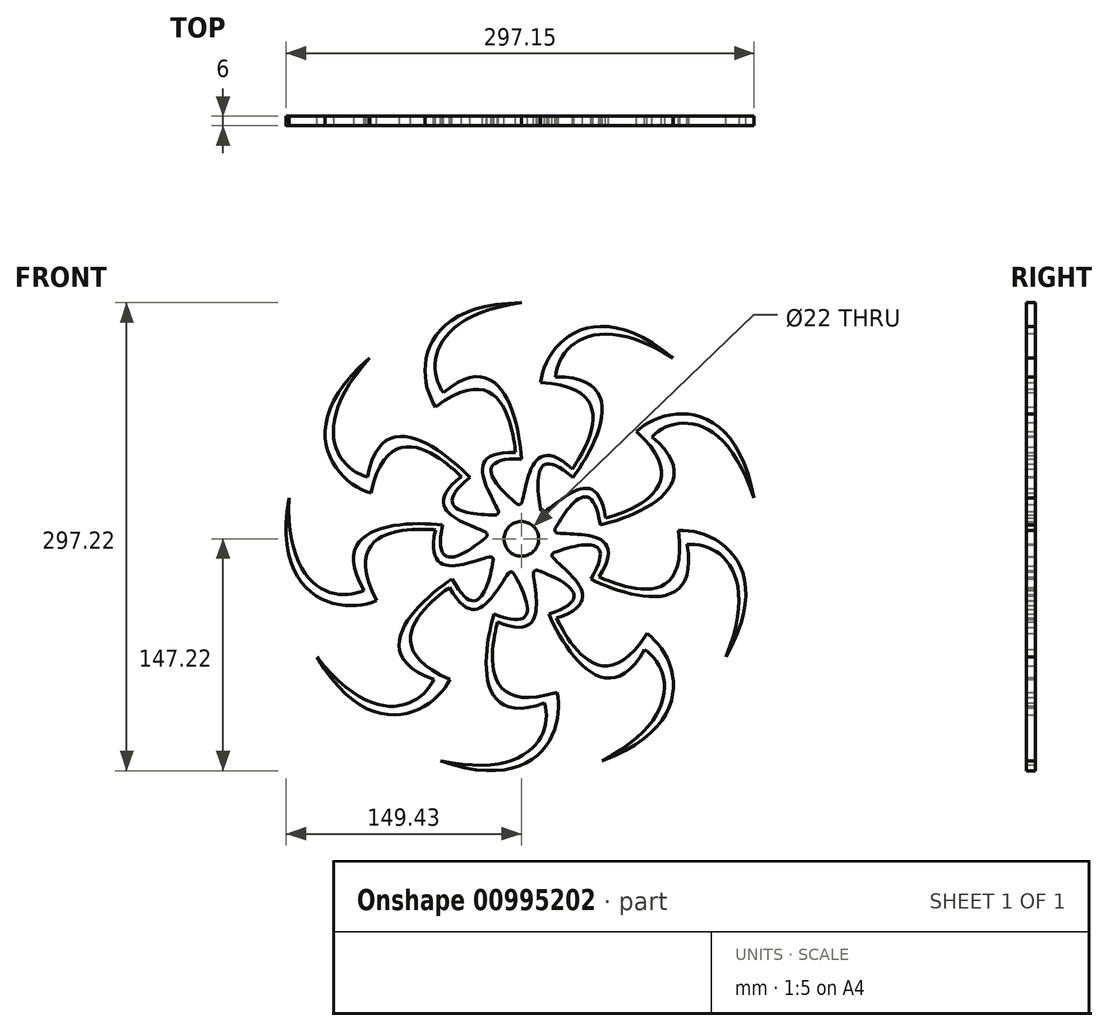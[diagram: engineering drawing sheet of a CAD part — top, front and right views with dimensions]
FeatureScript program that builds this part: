
annotation { "Feature Type Name" : "Feature", "Feature Type Description" : "" }
export const myFeature = defineFeature(function(context is Context, id is Id, definition is map)
    precondition{}
    {
        {
            var Q0;
            Q0=qCreatedBy(makeId("Front.planeOp"),FACE);
            var sketch = newSketch(context, id + "F0", { "sketchPlane" : qUnion([Q0])});
            skCircle(sketch, "E0", {"center": v(0, 0) * mm, "radius": 11 * mm});
            skCircle(sketch, "E1", {"center": v(0, 0) * mm, "radius": 20 * mm});
            skCircle(sketch, "E2", {"center": v(0, 0) * mm, "radius": 150 * mm, "construction": true});
            skCircle(sketch, "E3", {"center": v(0, 0) * mm, "radius": 100 * mm, "construction": true});
            skCircle(sketch, "E4", {"center": v(0, 0) * mm, "radius": 55 * mm, "construction": true});
            skLineSegment(sketch, "E5", {"start": v(0, 0) * mm, "end": v(0, 150) * mm, "construction": true});
            skLineSegment(sketch, "E6", {"start": v(0, 0) * mm, "end": v(-150, 0) * mm, "construction": true});
            skFitSpline(sketch, "E7", {"points": [v(0, 150) * mm, v(-54.5, 83.84) * mm], "startDerivative": vector(-202.47, -1.9) * mm, "endDerivative": vector(38.9, -57.48) * mm});
            skFitSpline(sketch, "E8", {"points": [v(0, 150) * mm, v(-49.5, 92.84) * mm], "startDerivative": vector(-175.37, -24.85) * mm, "endDerivative": vector(34.14, -48.17) * mm});
            skFitSpline(sketch, "E9", {"points": [v(-54.5, 83.84) * mm, v(-3.77, 54.87) * mm], "startDerivative": vector(133.54, 101.9) * mm, "endDerivative": vector(3.69, -31.33) * mm});
            skFitSpline(sketch, "E10", {"points": [v(-3.77, 54.87) * mm, v(-13.71, 14.56) * mm], "startDerivative": vector(-120.75, 4.76) * mm, "endDerivative": vector(0.9, -24.6) * mm});
            skFitSpline(sketch, "E11", {"points": [v(-49.5, 92.84) * mm, v(0, 50.87) * mm], "startDerivative": vector(109.95, 93.55) * mm, "endDerivative": vector(4.78, -77.47) * mm});
            skFitSpline(sketch, "E12", {"points": [v(0, 50.87) * mm, v(0, 20) * mm], "startDerivative": vector(-109.89, 3.26) * mm, "endDerivative": vector(36.75, -28.8) * mm});
            skSolve(sketch);
        }
        {
            var Q0;
            Q0=qCreatedBy(makeId("Right.planeOp"),FACE);
            var sketch = newSketch(context, id + "F1", { "sketchPlane" : qUnion([Q0])});
            skLineSegment(sketch, "E13", {"start": v(0, 0) * mm, "end": v(-50, 0) * mm, "construction": true});
            skSolve(sketch);
        }
        {
            var Q0;
            Q0=makeQuery(id+"F0.imprint","IMPRINT",FACE,{"disambiguationData":[TD([[makeQuery(id+"F0.imprint","IMPRINT",EDGE,{"derivedFrom":sQuery(id+"F0.wireOp",EDGE,"E0")}),-1.0]])]});
            extrude(context, id + "F2", {"entities" : qUnion([Q0]), "depth" : 6 * mm, "offsetDistance" : 25 * mm});
        }
        {
            var Q0;
            Q0=makeQuery(id+"F0.imprint","IMPRINT",FACE,{"disambiguationData":[TD([[makeQuery(id+"F0.imprint","IMPRINT",EDGE,{"derivedFrom":sQuery(id+"F0.wireOp",EDGE,"E7")}),1.0]])]});
            extrude(context, id + "F3", {"entities" : qUnion([Q0]), "depth" : 6 * mm, "offsetDistance" : 25 * mm});
        }
        {
            var Q0;
            Q0=makeQuery(id+"F3.opExtrude","SWEPT_BODY",BODY,{"disambiguationData":[OSD([sQuery(id+"F0.wireOp",EDGE,"E1"),sQuery(id+"F0.wireOp",EDGE,"E7"),sQuery(id+"F0.wireOp",EDGE,"E8"),sQuery(id+"F0.wireOp",EDGE,"E9"),sQuery(id+"F0.wireOp",EDGE,"E10"),sQuery(id+"F0.wireOp",EDGE,"E11"),sQuery(id+"F0.wireOp",EDGE,"E12")])]});
            var Q1;
            Q1=sQuery(id+"F1.wireOp",EDGE,"E13");
            circularPattern(context, id + "F4", {"operationType" : NewBodyOperationType.ADD, "entities" : qUnion([Q0]), "axis" : qUnion([Q1]), "angle" : 360 * degree, "instanceCount" : 9, "equalSpace" : true});
        }
        {
            var Q0;
            Q0=makeQuery(id+"F4.boolean.opBoolean","INTERSECT",EDGE,{"derivedFrom":[makeQuery(id+"F4.opPattern","COPY",FACE,{"derivedFrom":makeQuery(id+"F3.opExtrude","SWEPT_FACE",FACE,{"disambiguationData":[OSD([sQuery(id+"F0.wireOp",EDGE,"E10")])]}),"instanceName":"7"}),makeQuery(id+"F4.opPattern","COPY",FACE,{"derivedFrom":makeQuery(id+"F3.opExtrude","SWEPT_FACE",FACE,{"disambiguationData":[OSD([sQuery(id+"F0.wireOp",EDGE,"E12")])]}),"instanceName":"8"})]});
            var Q1;
            Q1=makeQuery(id+"F4.boolean.opBoolean","INTERSECT",EDGE,{"derivedFrom":[makeQuery(id+"F4.opPattern","COPY",FACE,{"derivedFrom":makeQuery(id+"F3.opExtrude","SWEPT_FACE",FACE,{"disambiguationData":[OSD([sQuery(id+"F0.wireOp",EDGE,"E10")])]}),"instanceName":"6"}),makeQuery(id+"F4.opPattern","COPY",FACE,{"derivedFrom":makeQuery(id+"F3.opExtrude","SWEPT_FACE",FACE,{"disambiguationData":[OSD([sQuery(id+"F0.wireOp",EDGE,"E12")])]}),"instanceName":"7"})]});
            var Q2;
            Q2=makeQuery(id+"F4.boolean.opBoolean","INTERSECT",EDGE,{"derivedFrom":[makeQuery(id+"F4.opPattern","COPY",FACE,{"derivedFrom":makeQuery(id+"F3.opExtrude","SWEPT_FACE",FACE,{"disambiguationData":[OSD([sQuery(id+"F0.wireOp",EDGE,"E10")])]}),"instanceName":"5"}),makeQuery(id+"F4.opPattern","COPY",FACE,{"derivedFrom":makeQuery(id+"F3.opExtrude","SWEPT_FACE",FACE,{"disambiguationData":[OSD([sQuery(id+"F0.wireOp",EDGE,"E12")])]}),"instanceName":"6"})]});
            var Q3;
            Q3=makeQuery(id+"F4.boolean.opBoolean","INTERSECT",EDGE,{"derivedFrom":[makeQuery(id+"F4.opPattern","COPY",FACE,{"derivedFrom":makeQuery(id+"F3.opExtrude","SWEPT_FACE",FACE,{"disambiguationData":[OSD([sQuery(id+"F0.wireOp",EDGE,"E10")])]}),"instanceName":"4"}),makeQuery(id+"F4.opPattern","COPY",FACE,{"derivedFrom":makeQuery(id+"F3.opExtrude","SWEPT_FACE",FACE,{"disambiguationData":[OSD([sQuery(id+"F0.wireOp",EDGE,"E12")])]}),"instanceName":"5"})]});
            var Q4;
            Q4=makeQuery(id+"F4.boolean.opBoolean","INTERSECT",EDGE,{"derivedFrom":[makeQuery(id+"F4.opPattern","COPY",FACE,{"derivedFrom":makeQuery(id+"F3.opExtrude","SWEPT_FACE",FACE,{"disambiguationData":[OSD([sQuery(id+"F0.wireOp",EDGE,"E10")])]}),"instanceName":"3"}),makeQuery(id+"F4.opPattern","COPY",FACE,{"derivedFrom":makeQuery(id+"F3.opExtrude","SWEPT_FACE",FACE,{"disambiguationData":[OSD([sQuery(id+"F0.wireOp",EDGE,"E12")])]}),"instanceName":"4"})]});
            var Q5;
            Q5=makeQuery(id+"F4.boolean.opBoolean","INTERSECT",EDGE,{"derivedFrom":[makeQuery(id+"F4.opPattern","COPY",FACE,{"derivedFrom":makeQuery(id+"F3.opExtrude","SWEPT_FACE",FACE,{"disambiguationData":[OSD([sQuery(id+"F0.wireOp",EDGE,"E10")])]}),"instanceName":"2"}),makeQuery(id+"F4.opPattern","COPY",FACE,{"derivedFrom":makeQuery(id+"F3.opExtrude","SWEPT_FACE",FACE,{"disambiguationData":[OSD([sQuery(id+"F0.wireOp",EDGE,"E12")])]}),"instanceName":"3"})]});
            var Q6;
            Q6=makeQuery(id+"F4.boolean.opBoolean","INTERSECT",EDGE,{"derivedFrom":[makeQuery(id+"F4.opPattern","COPY",FACE,{"derivedFrom":makeQuery(id+"F3.opExtrude","SWEPT_FACE",FACE,{"disambiguationData":[OSD([sQuery(id+"F0.wireOp",EDGE,"E10")])]}),"instanceName":"1"}),makeQuery(id+"F4.opPattern","COPY",FACE,{"derivedFrom":makeQuery(id+"F3.opExtrude","SWEPT_FACE",FACE,{"disambiguationData":[OSD([sQuery(id+"F0.wireOp",EDGE,"E12")])]}),"instanceName":"2"})]});
            var Q7;
            Q7=makeQuery(id+"F4.boolean.opBoolean","INTERSECT",EDGE,{"derivedFrom":[makeQuery(id+"F3.opExtrude","SWEPT_FACE",FACE,{"disambiguationData":[OSD([sQuery(id+"F0.wireOp",EDGE,"E10")])]}),makeQuery(id+"F4.opPattern","COPY",FACE,{"derivedFrom":makeQuery(id+"F3.opExtrude","SWEPT_FACE",FACE,{"disambiguationData":[OSD([sQuery(id+"F0.wireOp",EDGE,"E12")])]}),"instanceName":"1"})]});
            var Q8;
            Q8=makeQuery(id+"F4.boolean.opBoolean","INTERSECT",EDGE,{"derivedFrom":[makeQuery(id+"F3.opExtrude","SWEPT_FACE",FACE,{"disambiguationData":[OSD([sQuery(id+"F0.wireOp",EDGE,"E12")])]}),makeQuery(id+"F4.opPattern","COPY",FACE,{"derivedFrom":makeQuery(id+"F3.opExtrude","SWEPT_FACE",FACE,{"disambiguationData":[OSD([sQuery(id+"F0.wireOp",EDGE,"E10")])]}),"instanceName":"8"})]});
            fillet(context, id + "F5", {"entities" : qUnion([Q0, Q1, Q2, Q3, Q4, Q5, Q6, Q7, Q8]), "radius" : 2 * mm, "tangentPropagation" : true, "allowEdgeOverflow" : false});
        }
    });
